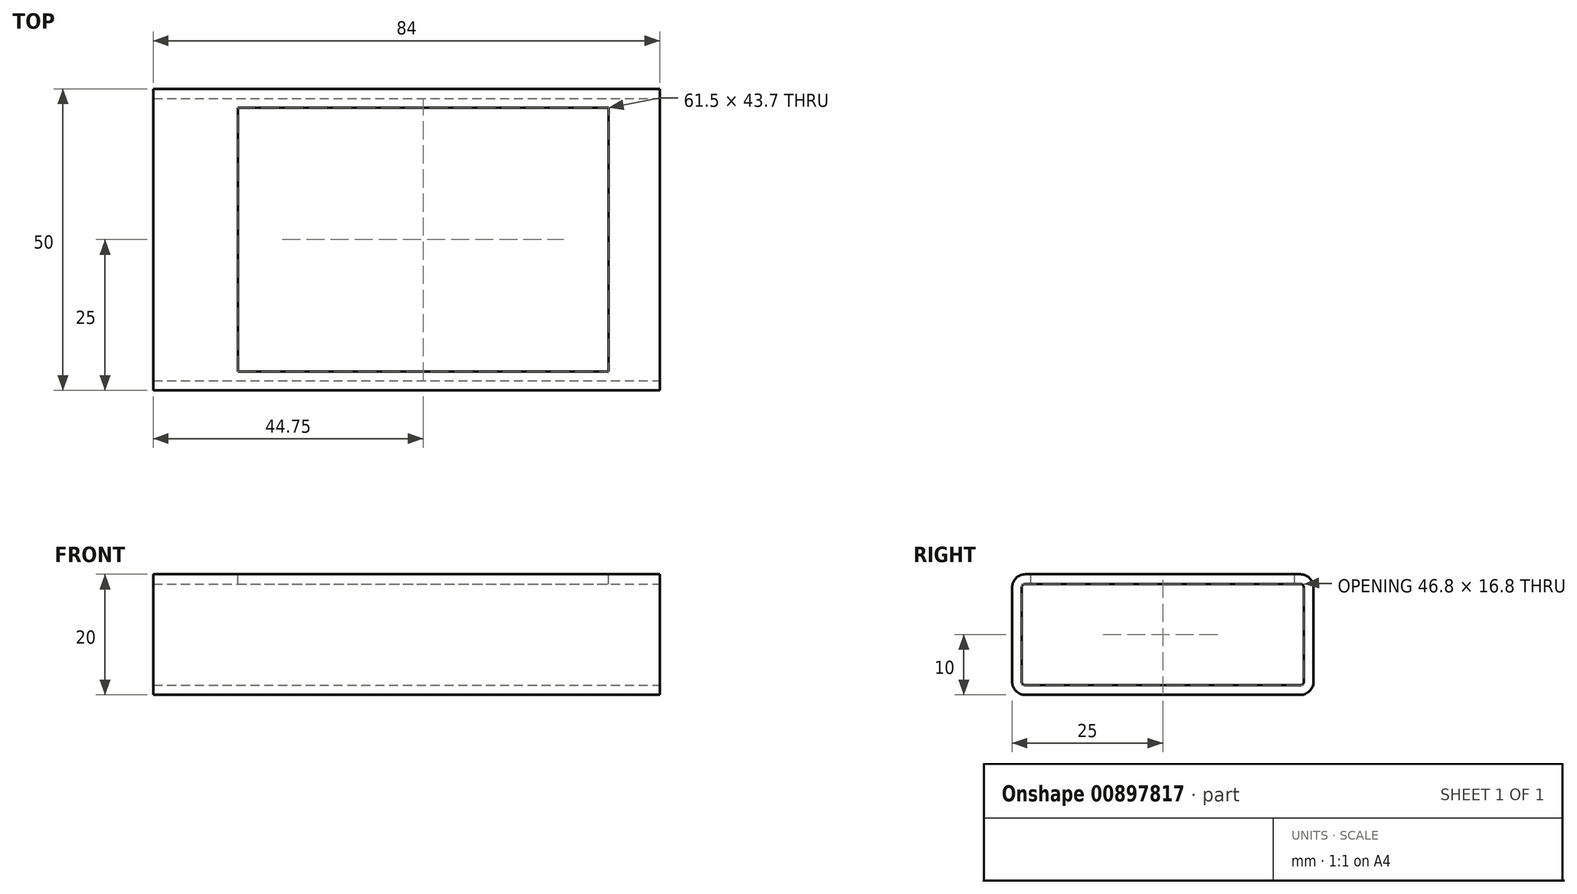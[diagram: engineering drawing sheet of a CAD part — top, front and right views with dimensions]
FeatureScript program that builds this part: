
annotation { "Feature Type Name" : "Feature", "Feature Type Description" : "" }
export const myFeature = defineFeature(function(context is Context, id is Id, definition is map)
    precondition{}
    {
        {
            var Q0;
            Q0=qCreatedBy(makeId("Right.planeOp"),FACE);
            var sketch = newSketch(context, id + "F0", { "sketchPlane" : qUnion([Q0])});
            skLineSegment(sketch, "E0.bottom", {"start": v(2.2, 20) * mm, "end": v(47.8, 20) * mm});
            skLineSegment(sketch, "E0.top", {"start": v(2.2, 0) * mm, "end": v(47.8, 0) * mm});
            skLineSegment(sketch, "E0.left", {"start": v(0, 17.8) * mm, "end": v(0, 2.2) * mm});
            skLineSegment(sketch, "E0.right", {"start": v(50, 17.8) * mm, "end": v(50, 2.2) * mm});
            skPoint(sketch, "E1.visualSharp", {"position": v(0, 20) * mm});
            skArc(sketch, "E1.filletArc", {"start": v(2.2, 20) * mm, "mid": v(0.64, 19.36) * mm, "end": v(0, 17.8) * mm});
            skPoint(sketch, "E2.visualSharp", {"position": v(50, 20) * mm});
            skArc(sketch, "E2.filletArc", {"start": v(50, 17.8) * mm, "mid": v(49.36, 19.36) * mm, "end": v(47.8, 20) * mm});
            skPoint(sketch, "E3.visualSharp", {"position": v(50, 0) * mm});
            skArc(sketch, "E3.filletArc", {"start": v(47.8, 0) * mm, "mid": v(49.36, 0.64) * mm, "end": v(50, 2.2) * mm});
            skPoint(sketch, "E4.visualSharp", {"position": v(0, 0) * mm});
            skArc(sketch, "E4.filletArc", {"start": v(0, 2.2) * mm, "mid": v(0.64, 0.64) * mm, "end": v(2.2, 0) * mm});
            skArc(sketch, "E5.0", {"start": v(48.4, 17.8) * mm, "mid": v(48.22, 18.22) * mm, "end": v(47.8, 18.4) * mm});
            skLineSegment(sketch, "E5.1", {"start": v(2.2, 18.4) * mm, "end": v(47.8, 18.4) * mm});
            skLineSegment(sketch, "E5.2", {"start": v(48.4, 17.8) * mm, "end": v(48.4, 2.2) * mm});
            skArc(sketch, "E5.3", {"start": v(2.2, 18.4) * mm, "mid": v(1.78, 18.22) * mm, "end": v(1.6, 17.8) * mm});
            skArc(sketch, "E5.4", {"start": v(47.8, 1.6) * mm, "mid": v(48.22, 1.78) * mm, "end": v(48.4, 2.2) * mm});
            skLineSegment(sketch, "E5.5", {"start": v(2.2, 1.6) * mm, "end": v(47.8, 1.6) * mm});
            skArc(sketch, "E5.6", {"start": v(1.6, 2.2) * mm, "mid": v(1.78, 1.78) * mm, "end": v(2.2, 1.6) * mm});
            skLineSegment(sketch, "E5.7", {"start": v(1.6, 17.8) * mm, "end": v(1.6, 2.2) * mm});
            skSolve(sketch);
        }
        {
            var Q0;
            Q0=makeQuery(id+"F0.imprint","IMPRINT",FACE,{"disambiguationData":[TD([[makeQuery(id+"F0.imprint","IMPRINT",EDGE,{"derivedFrom":sQuery(id+"F0.wireOp",EDGE,"E0.bottom")}),-1.0]])]});
            extrude(context, id + "F1", {"entities" : qUnion([Q0]), "oppositeDirection" : true, "depth" : 84 * mm, "offsetDistance" : 25 * mm});
        }
        {
            var Q0;
            Q0=makeQuery(id+"F1.opExtrude","SWEPT_FACE",FACE,{"disambiguationData":[OSD([sQuery(id+"F0.wireOp",EDGE,"E0.bottom")])]});
            var sketch = newSketch(context, id + "F2", { "sketchPlane" : qUnion([Q0])});
            skLineSegment(sketch, "E6.bottom", {"start": v(-70, 46.85) * mm, "end": v(-8.5, 46.85) * mm});
            skLineSegment(sketch, "E6.top", {"start": v(-70, 3.15) * mm, "end": v(-8.5, 3.15) * mm});
            skLineSegment(sketch, "E6.left", {"start": v(-70, 46.85) * mm, "end": v(-70, 3.15) * mm});
            skLineSegment(sketch, "E6.right", {"start": v(-8.5, 46.85) * mm, "end": v(-8.5, 3.15) * mm});
            skSolve(sketch);
        }
        {
            var Q0;
            Q0=makeQuery(id+"F2.imprint","IMPRINT",FACE,{"disambiguationData":[TD([[makeQuery(id+"F2.imprint","IMPRINT",EDGE,{"derivedFrom":sQuery(id+"F2.wireOp",EDGE,"E6.bottom")}),-1.0]])]});
            extrude(context, id + "F3", {"entities" : qUnion([Q0]), "operationType" : NewBodyOperationType.REMOVE, "endBound" : BoundingType.UP_TO_NEXT, "oppositeDirection" : true, "depth" : 25 * mm, "offsetDistance" : 25 * mm});
        }
    });
